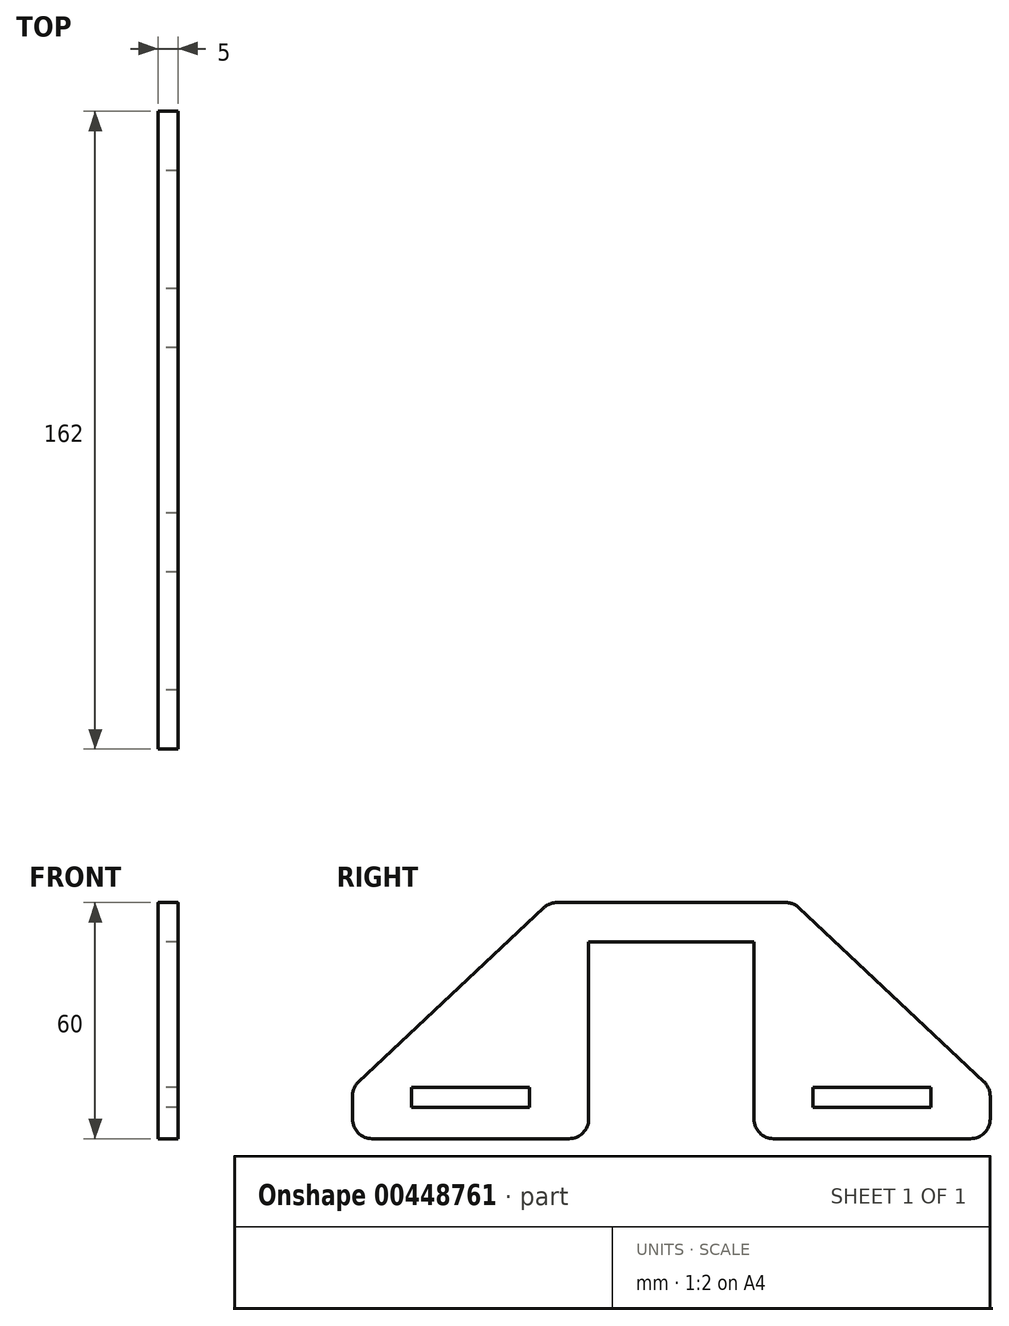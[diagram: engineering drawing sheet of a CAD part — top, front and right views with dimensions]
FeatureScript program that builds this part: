
annotation { "Feature Type Name" : "Feature", "Feature Type Description" : "" }
export const myFeature = defineFeature(function(context is Context, id is Id, definition is map)
    precondition{}
    {
        {
            var Q0;
            Q0=qCreatedBy(makeId("Right.planeOp"),FACE);
            var sketch = newSketch(context, id + "F0", { "sketchPlane" : qUnion([Q0])});
            skLineSegment(sketch, "E0", {"start": v(0, 5) * mm, "end": v(0, 50) * mm});
            skLineSegment(sketch, "E1", {"start": v(0, 50) * mm, "end": v(42, 50) * mm});
            skLineSegment(sketch, "E2", {"start": v(42, 50) * mm, "end": v(42, 5) * mm});
            skLineSegment(sketch, "E3", {"start": v(-5, 0) * mm, "end": v(-55, 0) * mm});
            skLineSegment(sketch, "E4", {"start": v(-60, 5) * mm, "end": v(-60, 10.84) * mm});
            skLineSegment(sketch, "E5", {"start": v(-60, 8) * mm, "end": v(0, 8) * mm, "construction": true});
            skLineSegment(sketch, "E6.bottom", {"start": v(-45, 8) * mm, "end": v(-15, 8) * mm});
            skLineSegment(sketch, "E6.top", {"start": v(-45, 13) * mm, "end": v(-15, 13) * mm});
            skLineSegment(sketch, "E6.left", {"start": v(-45, 8) * mm, "end": v(-45, 13) * mm});
            skLineSegment(sketch, "E6.right", {"start": v(-15, 8) * mm, "end": v(-15, 13) * mm});
            skPoint(sketch, "E7", {"position": v(-30, 8) * mm});
            skPoint(sketch, "E8", {"position": v(-30, 0) * mm});
            skLineSegment(sketch, "E9", {"start": v(-8.02, 60) * mm, "end": v(50.02, 60) * mm});
            skLineSegment(sketch, "E10", {"start": v(-58.42, 14.48) * mm, "end": v(-11.44, 58.64) * mm});
            skPoint(sketch, "E11.visualSharp", {"position": v(-10, 60) * mm});
            skArc(sketch, "E11.filletArc", {"start": v(-8.02, 60) * mm, "mid": v(-9.86, 59.65) * mm, "end": v(-11.44, 58.64) * mm});
            skLineSegment(sketch, "E12", {"start": v(21, 50) * mm, "end": v(21, 0) * mm, "construction": true});
            skLineSegment(sketch, "E13.MirrorCS", {"start": v(100.42, 14.48) * mm, "end": v(53.44, 58.64) * mm});
            skArc(sketch, "E14.MirrorCS", {"start": v(50.02, 60) * mm, "mid": v(51.86, 59.65) * mm, "end": v(53.44, 58.64) * mm});
            skLineSegment(sketch, "E15.MirrorCS", {"start": v(102, 5) * mm, "end": v(102, 10.84) * mm});
            skLineSegment(sketch, "E16.MirrorCS", {"start": v(47, 0) * mm, "end": v(97, 0) * mm});
            skLineSegment(sketch, "E17.MirrorCS", {"start": v(57, 8) * mm, "end": v(57, 13) * mm});
            skLineSegment(sketch, "E18.MirrorCS", {"start": v(87, 13) * mm, "end": v(57, 13) * mm});
            skLineSegment(sketch, "E19.MirrorCS", {"start": v(87, 8) * mm, "end": v(87, 13) * mm});
            skPoint(sketch, "E20.MirrorP", {"position": v(72, 8) * mm});
            skLineSegment(sketch, "E21.MirrorCS", {"start": v(87, 8) * mm, "end": v(57, 8) * mm});
            skPoint(sketch, "E22.visualSharp", {"position": v(0, 0) * mm});
            skArc(sketch, "E22.filletArc", {"start": v(-5, 0) * mm, "mid": v(-1.46, 1.46) * mm, "end": v(0, 5) * mm});
            skPoint(sketch, "E23.visualSharp", {"position": v(-60, 0) * mm});
            skArc(sketch, "E23.filletArc", {"start": v(-60, 5) * mm, "mid": v(-58.54, 1.46) * mm, "end": v(-55, 0) * mm});
            skPoint(sketch, "E24.visualSharp", {"position": v(42, 0) * mm});
            skArc(sketch, "E24.filletArc", {"start": v(42, 5) * mm, "mid": v(43.46, 1.46) * mm, "end": v(47, 0) * mm});
            skPoint(sketch, "E25.visualSharp", {"position": v(102, 0) * mm});
            skArc(sketch, "E25.filletArc", {"start": v(97, 0) * mm, "mid": v(100.54, 1.46) * mm, "end": v(102, 5) * mm});
            skPoint(sketch, "E26.visualSharp", {"position": v(-60, 13) * mm});
            skArc(sketch, "E26.filletArc", {"start": v(-58.42, 14.48) * mm, "mid": v(-59.59, 12.82) * mm, "end": v(-60, 10.84) * mm});
            skPoint(sketch, "E27.visualSharp", {"position": v(102, 13) * mm});
            skArc(sketch, "E27.filletArc", {"start": v(102, 10.84) * mm, "mid": v(101.59, 12.82) * mm, "end": v(100.42, 14.48) * mm});
            skSolve(sketch);
        }
        {
            var Q0;
            Q0=qSketchRegion(id+"F0",true);
            extrude(context, id + "F1", {"entities" : qUnion([Q0]), "depth" : 5 * mm});
        }
    });
